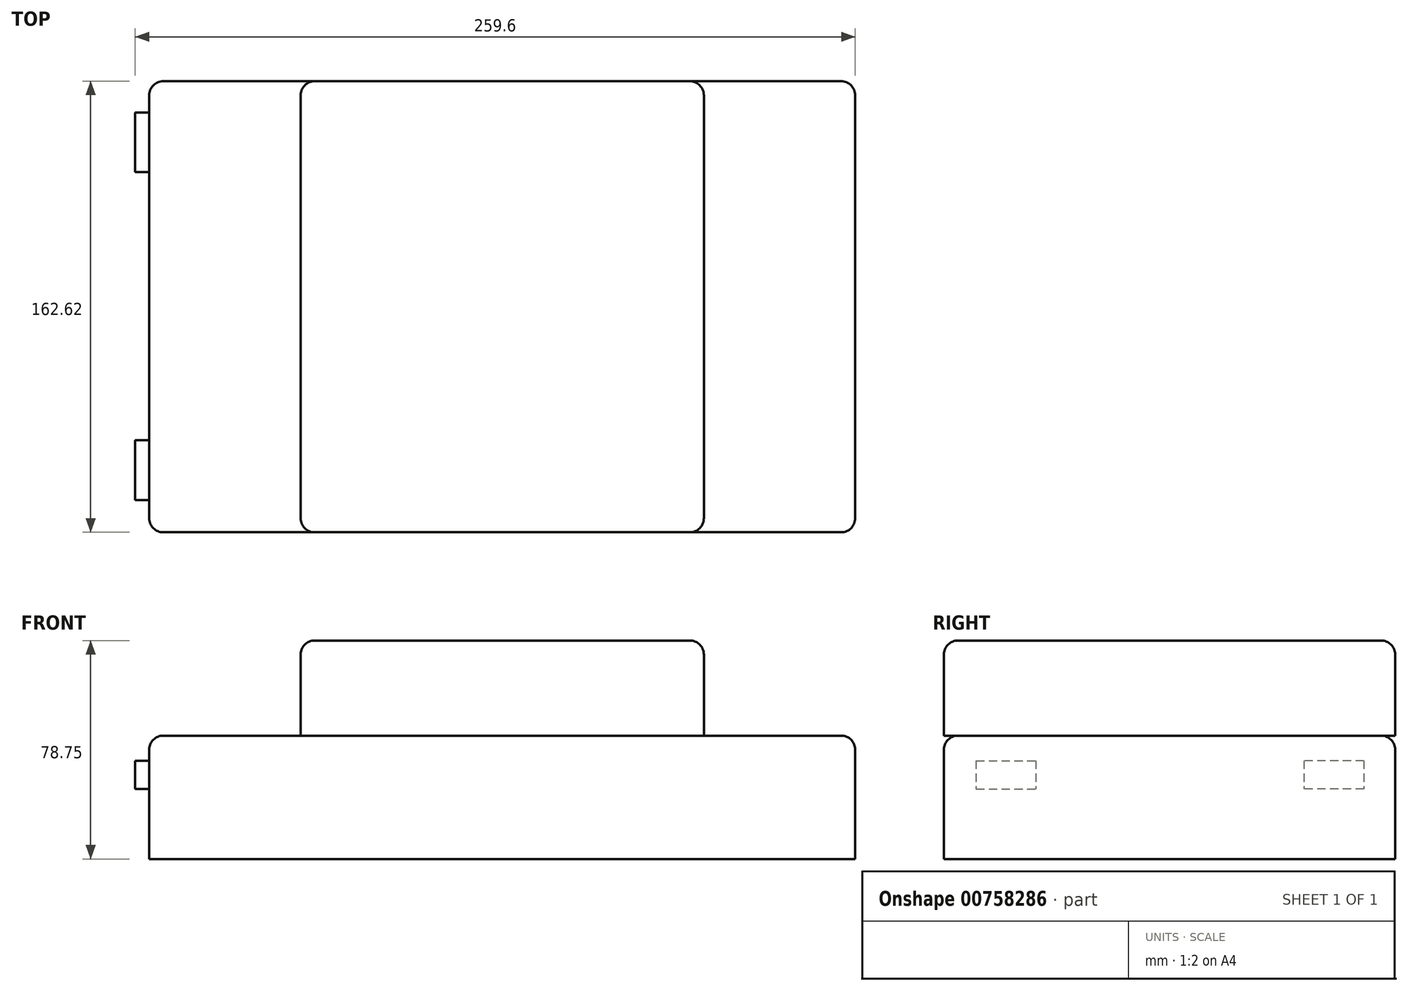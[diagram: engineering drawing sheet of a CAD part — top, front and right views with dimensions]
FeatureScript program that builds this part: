
annotation { "Feature Type Name" : "Feature", "Feature Type Description" : "" }
export const myFeature = defineFeature(function(context is Context, id is Id, definition is map)
    precondition{}
    {
        {
            var Q0;
            Q0=qCreatedBy(makeId("Top.planeOp"),FACE);
            var sketch = newSketch(context, id + "F0", { "sketchPlane" : qUnion([Q0])});
            skLineSegment(sketch, "E0.bottom", {"start": v(-127.26, 81.3) * mm, "end": v(127.26, 81.3) * mm});
            skLineSegment(sketch, "E0.top", {"start": v(-127.26, -81.3) * mm, "end": v(127.26, -81.3) * mm});
            skLineSegment(sketch, "E0.left", {"start": v(-127.26, 81.3) * mm, "end": v(-127.26, -81.3) * mm});
            skLineSegment(sketch, "E0.right", {"start": v(127.26, 81.3) * mm, "end": v(127.26, -81.3) * mm});
            skPoint(sketch, "E0.middle", {"position": v(0, 0) * mm});
            skSolve(sketch);
        }
        {
            var Q0;
            Q0=makeQuery(id+"F0.imprint","IMPRINT",FACE,{"disambiguationData":[TD([[makeQuery(id+"F0.imprint","IMPRINT",EDGE,{"derivedFrom":sQuery(id+"F0.wireOp",EDGE,"E0.bottom")}),-1.0]])]});
            extrude(context, id + "F1", {"entities" : qUnion([Q0]), "endBound" : BoundingType.SYMMETRIC, "depth" : 44.45 * mm, "offsetDistance" : 25.4 * mm});
        }
        {
            var Q0;
            Q0=makeQuery(id+"F1.opExtrude","CAP_FACE",FACE,{"disambiguationData":[OSD([sQuery(id+"F0.wireOp",EDGE,"E0.bottom"),sQuery(id+"F0.wireOp",EDGE,"E0.top"),sQuery(id+"F0.wireOp",EDGE,"E0.left"),sQuery(id+"F0.wireOp",EDGE,"E0.right")])],"isStart":false});
            var sketch = newSketch(context, id + "F2", { "sketchPlane" : qUnion([Q0])});
            skLineSegment(sketch, "E1.bottom", {"start": v(-72.69, 81.3) * mm, "end": v(72.69, 81.3) * mm});
            skLineSegment(sketch, "E1.top", {"start": v(-72.69, -81.3) * mm, "end": v(72.69, -81.3) * mm});
            skLineSegment(sketch, "E1.left", {"start": v(-72.69, 81.3) * mm, "end": v(-72.69, -81.3) * mm});
            skLineSegment(sketch, "E1.right", {"start": v(72.69, 81.3) * mm, "end": v(72.69, -81.3) * mm});
            skPoint(sketch, "E1.middle", {"position": v(0, 0) * mm});
            skSolve(sketch);
        }
        {
            var Q0;
            Q0=makeQuery(id+"F2.imprint","IMPRINT",FACE,{"disambiguationData":[TD([[makeQuery(id+"F2.imprint","IMPRINT",EDGE,{"derivedFrom":sQuery(id+"F2.wireOp",EDGE,"E1.bottom")}),-1.0]])]});
            var Q1;
            Q1=sQuery(id+"F2.wireOp",EDGE,"E1.top");
            extrude(context, id + "F3", {"entities" : qUnion([Q0]), "surfaceEntities" : qUnion([Q1]), "depth" : 34.3 * mm, "offsetDistance" : 25.4 * mm});
        }
        {
            var Q0;
            Q0=makeQuery(id+"F1.opExtrude","SWEPT_FACE",FACE,{"disambiguationData":[OSD([sQuery(id+"F0.wireOp",EDGE,"E0.top")])]});
            var sketch = newSketch(context, id + "F4", { "sketchPlane" : qUnion([Q0])});
            skLineSegment(sketch, "E2", {"start": v(0, -22.23) * mm, "end": v(0, 54.67) * mm});
            skSolve(sketch);
        }
        {
            var Q0;
            Q0=makeQuery(id+"F3.opExtrude","SWEPT_FACE",FACE,{"disambiguationData":[OSD([sQuery(id+"F2.wireOp",EDGE,"E1.top")])]});
            var sketch = newSketch(context, id + "F5", { "sketchPlane" : qUnion([Q0])});
            skLineSegment(sketch, "E3.bottom", {"start": v(-5.62, 51.3) * mm, "end": v(-67.73, 51.3) * mm});
            skLineSegment(sketch, "E3.top", {"start": v(-5.62, 22.23) * mm, "end": v(-67.73, 22.23) * mm});
            skLineSegment(sketch, "E3.left", {"start": v(-5.62, 51.3) * mm, "end": v(-5.62, 22.23) * mm});
            skLineSegment(sketch, "E3.right", {"start": v(-67.73, 51.3) * mm, "end": v(-67.73, 22.23) * mm});
            skSolve(sketch);
        }
        {
            var Q0;
            Q0=makeQuery(id+"F5.imprint","IMPRINT",FACE,{"disambiguationData":[TD([[makeQuery(id+"F5.imprint","IMPRINT",EDGE,{"derivedFrom":sQuery(id+"F5.wireOp",EDGE,"E3.bottom")}),-1.0]])]});
            var sketch = newSketch(context, id + "F6", { "sketchPlane" : qUnion([Q0])});
            skLineSegment(sketch, "E4.bottom", {"start": v(8.14, 51.07) * mm, "end": v(67.27, 51.07) * mm});
            skLineSegment(sketch, "E4.top", {"start": v(8.14, 22.65) * mm, "end": v(67.27, 22.65) * mm});
            skLineSegment(sketch, "E4.left", {"start": v(8.14, 51.07) * mm, "end": v(8.14, 22.65) * mm});
            skLineSegment(sketch, "E4.right", {"start": v(67.27, 51.07) * mm, "end": v(67.27, 22.65) * mm});
            skSolve(sketch);
        }
        {
            var Q0;
            {var subQ1=sQuery(id+"F0.wireOp",EDGE,"E0.top");var subQ6=makeQuery(id+"F1.opExtrude","SWEPT_EDGE",EDGE,{"disambiguationData":[OSD([subQ1,sQuery(id+"F0.wireOp",EDGE,"E0.left")])]});Q0=makeQuery(id+"F4.imprint","IMPRINT",FACE,{"disambiguationData":[TD([[makeQuery(id+"F4.imprint","IMPRINT",EDGE,{"derivedFrom":subQ6}),1.0]])]});}
            var sketch = newSketch(context, id + "F7", { "sketchPlane" : qUnion([Q0])});
            skArc(sketch, "E5", {"start": v(-73, 22.65) * mm, "mid": v(-75.73, 0.38) * mm, "end": v(-75.52, -22.05) * mm});
            skSolve(sketch);
        }
        {
            var Q0;
            {var subQ1=sQuery(id+"F0.wireOp",EDGE,"E0.top");var subQ6=makeQuery(id+"F1.opExtrude","SWEPT_EDGE",EDGE,{"disambiguationData":[OSD([subQ1,sQuery(id+"F0.wireOp",EDGE,"E0.right")])]});Q0=makeQuery(id+"F4.imprint","IMPRINT",FACE,{"disambiguationData":[TD([[makeQuery(id+"F4.imprint","IMPRINT",EDGE,{"derivedFrom":subQ6}),-1.0]])]});}
            var sketch = newSketch(context, id + "F8", { "sketchPlane" : qUnion([Q0])});
            skArc(sketch, "E6", {"start": v(7.68, 16.46) * mm, "mid": v(12.46, 15) * mm, "end": v(17.3, 16.23) * mm});
            skSolve(sketch);
        }
        {
            var Q0;
            Q0=makeQuery(id+"F3.opExtrude","CAP_EDGE",EDGE,{"disambiguationData":[OSD([sQuery(id+"F2.wireOp",EDGE,"E1.top")])],"isStart":false});
            var Q1;
            Q1=makeQuery(id+"F3.opExtrude","SWEPT_EDGE",EDGE,{"disambiguationData":[OSD([sQuery(id+"F0.wireOp",EDGE,"E0.top"),sQuery(id+"F2.wireOp",EDGE,"E1.top"),sQuery(id+"F2.wireOp",EDGE,"E1.left")])]});
            var Q2;
            Q2=makeQuery(id+"F3.opExtrude","SWEPT_EDGE",EDGE,{"disambiguationData":[OSD([sQuery(id+"F0.wireOp",EDGE,"E0.top"),sQuery(id+"F2.wireOp",EDGE,"E1.top"),sQuery(id+"F2.wireOp",EDGE,"E1.right")])]});
            fillet(context, id + "F9", {"entities" : qUnion([Q0, Q1, Q2]), "radius" : 5.08 * mm, "tangentPropagation" : true, "allowEdgeOverflow" : false});
        }
        {
            var Q0;
            Q0=makeQuery(id+"F1.opExtrude","CAP_EDGE",EDGE,{"disambiguationData":[OSD([sQuery(id+"F0.wireOp",EDGE,"E0.top")])],"isStart":false});
            var Q1;
            Q1=makeQuery(id+"F1.opExtrude","SWEPT_EDGE",EDGE,{"disambiguationData":[OSD([sQuery(id+"F0.wireOp",EDGE,"E0.top"),sQuery(id+"F0.wireOp",EDGE,"E0.left")])]});
            var Q2;
            Q2=makeQuery(id+"F1.opExtrude","SWEPT_EDGE",EDGE,{"disambiguationData":[OSD([sQuery(id+"F0.wireOp",EDGE,"E0.top"),sQuery(id+"F0.wireOp",EDGE,"E0.right")])]});
            fillet(context, id + "F10", {"entities" : qUnion([Q0, Q1, Q2]), "radius" : 5.08 * mm, "tangentPropagation" : true, "allowEdgeOverflow" : false});
        }
        {
            var Q0;
            Q0=makeQuery(id+"F3.opExtrude","CAP_EDGE",EDGE,{"disambiguationData":[OSD([sQuery(id+"F2.wireOp",EDGE,"E1.left")])],"isStart":false});
            var Q1;
            Q1=makeQuery(id+"F3.opExtrude","SWEPT_EDGE",EDGE,{"disambiguationData":[OSD([sQuery(id+"F0.wireOp",EDGE,"E0.bottom"),sQuery(id+"F2.wireOp",EDGE,"E1.bottom"),sQuery(id+"F2.wireOp",EDGE,"E1.left")])]});
            fillet(context, id + "F11", {"entities" : qUnion([Q0, Q1]), "radius" : 5.08 * mm, "tangentPropagation" : true, "allowEdgeOverflow" : false});
        }
        {
            var Q0;
            Q0=makeQuery(id+"F1.opExtrude","CAP_EDGE",EDGE,{"disambiguationData":[OSD([sQuery(id+"F0.wireOp",EDGE,"E0.left")])],"isStart":false});
            var Q1;
            Q1=makeQuery(id+"F1.opExtrude","SWEPT_EDGE",EDGE,{"disambiguationData":[OSD([sQuery(id+"F0.wireOp",EDGE,"E0.bottom"),sQuery(id+"F0.wireOp",EDGE,"E0.left")])]});
            var Q2;
            Q2=makeQuery(id+"F1.opExtrude","CAP_EDGE",EDGE,{"disambiguationData":[OSD([sQuery(id+"F0.wireOp",EDGE,"E0.bottom")])],"isStart":false});
            fillet(context, id + "F12", {"entities" : qUnion([Q0, Q1, Q2]), "radius" : 5.08 * mm, "tangentPropagation" : true, "allowEdgeOverflow" : false});
        }
        {
            var Q0;
            Q0=makeQuery(id+"F3.opExtrude","CAP_EDGE",EDGE,{"disambiguationData":[OSD([sQuery(id+"F2.wireOp",EDGE,"E1.right")])],"isStart":false});
            var Q1;
            Q1=makeQuery(id+"F3.opExtrude","SWEPT_EDGE",EDGE,{"disambiguationData":[OSD([sQuery(id+"F0.wireOp",EDGE,"E0.bottom"),sQuery(id+"F2.wireOp",EDGE,"E1.bottom"),sQuery(id+"F2.wireOp",EDGE,"E1.right")])]});
            var Q2;
            Q2=makeQuery(id+"F3.opExtrude","CAP_EDGE",EDGE,{"disambiguationData":[OSD([sQuery(id+"F2.wireOp",EDGE,"E1.bottom")])],"isStart":false});
            var Q3;
            Q3=makeQuery(id+"F1.opExtrude","CAP_EDGE",EDGE,{"disambiguationData":[OSD([sQuery(id+"F0.wireOp",EDGE,"E0.right")])],"isStart":false});
            fillet(context, id + "F13", {"entities" : qUnion([Q0, Q1, Q2, Q3]), "radius" : 5.08 * mm, "tangentPropagation" : true, "allowEdgeOverflow" : false});
        }
        {
            var Q0;
            Q0=makeQuery(id+"F1.opExtrude","SWEPT_FACE",FACE,{"disambiguationData":[OSD([sQuery(id+"F0.wireOp",EDGE,"E0.left")])]});
            var sketch = newSketch(context, id + "F14", { "sketchPlane" : qUnion([Q0])});
            skLineSegment(sketch, "E7.bottom", {"start": v(-70.06, 13.2) * mm, "end": v(-48.48, 13.2) * mm});
            skLineSegment(sketch, "E7.top", {"start": v(-70.06, 3.04) * mm, "end": v(-48.48, 3.04) * mm});
            skLineSegment(sketch, "E7.left", {"start": v(-70.06, 13.2) * mm, "end": v(-70.06, 3.04) * mm});
            skLineSegment(sketch, "E7.right", {"start": v(-48.48, 13.2) * mm, "end": v(-48.48, 3.04) * mm});
            skLineSegment(sketch, "E8.bottom", {"start": v(69.74, 13.2) * mm, "end": v(48.16, 13.2) * mm});
            skLineSegment(sketch, "E8.top", {"start": v(69.74, 3.04) * mm, "end": v(48.16, 3.04) * mm});
            skLineSegment(sketch, "E8.left", {"start": v(69.74, 13.2) * mm, "end": v(69.74, 3.04) * mm});
            skLineSegment(sketch, "E8.right", {"start": v(48.16, 13.2) * mm, "end": v(48.16, 3.04) * mm});
            skSolve(sketch);
        }
        {
            var Q0;
            Q0=makeQuery(id+"F14.imprint","IMPRINT",FACE,{"disambiguationData":[TD([[makeQuery(id+"F14.imprint","IMPRINT",EDGE,{"derivedFrom":sQuery(id+"F14.wireOp",EDGE,"E7.bottom")}),-1.0]])]});
            var Q1;
            Q1=makeQuery(id+"F14.imprint","IMPRINT",FACE,{"disambiguationData":[TD([[makeQuery(id+"F14.imprint","IMPRINT",EDGE,{"derivedFrom":sQuery(id+"F14.wireOp",EDGE,"E8.bottom")}),1.0]])]});
            extrude(context, id + "F15", {"entities" : qUnion([Q0, Q1]), "operationType" : NewBodyOperationType.ADD, "depth" : 5.08 * mm, "offsetDistance" : 25.4 * mm});
        }
    });
